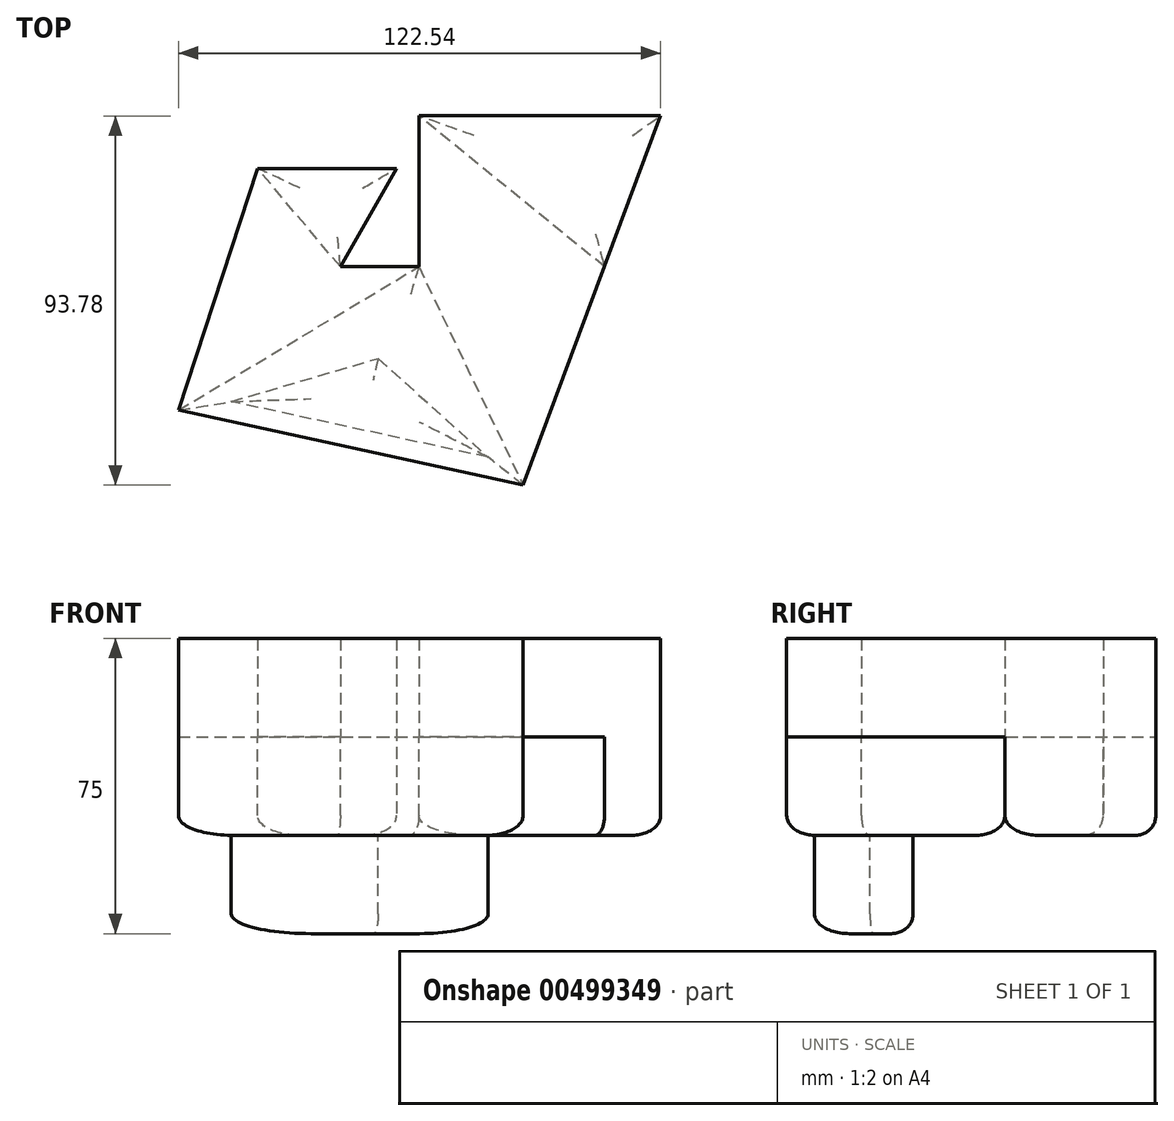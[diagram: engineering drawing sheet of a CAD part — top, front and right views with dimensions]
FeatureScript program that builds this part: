
annotation { "Feature Type Name" : "Feature", "Feature Type Description" : "" }
export const myFeature = defineFeature(function(context is Context, id is Id, definition is map)
    precondition{}
    {
        {
            var Q0;
            Q0=qCreatedBy(makeId("Top.planeOp"),FACE);
            var sketch = newSketch(context, id + "F0", { "sketchPlane" : qUnion([Q0])});
            skLineSegment(sketch, "E0", {"start": v(0, 0) * mm, "end": v(0, 38.34) * mm});
            skLineSegment(sketch, "E1", {"start": v(0, 38.34) * mm, "end": v(61.46, 38.34) * mm});
            skLineSegment(sketch, "E2", {"start": v(61.46, 38.34) * mm, "end": v(26.5, -55.44) * mm});
            skLineSegment(sketch, "E3", {"start": v(26.5, -55.44) * mm, "end": v(-61.08, -36.46) * mm});
            skLineSegment(sketch, "E4", {"start": v(-61.08, -36.46) * mm, "end": v(-40.97, 25) * mm});
            skLineSegment(sketch, "E5", {"start": v(-40.97, 25) * mm, "end": v(-5.64, 25) * mm});
            skLineSegment(sketch, "E6", {"start": v(-5.64, 25) * mm, "end": v(-19.92, 0) * mm});
            skLineSegment(sketch, "E7", {"start": v(-19.92, 0) * mm, "end": v(0, 0) * mm});
            skSolve(sketch);
        }
        {
            var Q0;
            Q0 = qSketchRegion(id + "F0", true);
            extrude(context, id + "F1", {"entities" : qUnion([Q0]), "depth" : 25 * mm});
        }
        {
            var Q0;
            Q0=makeQuery(id+"F1.opExtrude","CAP_FACE",FACE,{"disambiguationData":[OSD([sQuery(id+"F0.wireOp",EDGE,"E0"),sQuery(id+"F0.wireOp",EDGE,"E1"),sQuery(id+"F0.wireOp",EDGE,"E2"),sQuery(id+"F0.wireOp",EDGE,"E3"),sQuery(id+"F0.wireOp",EDGE,"E4"),sQuery(id+"F0.wireOp",EDGE,"E5"),sQuery(id+"F0.wireOp",EDGE,"E6"),sQuery(id+"F0.wireOp",EDGE,"E7")])],"isStart":true});
            var sketch = newSketch(context, id + "F2", { "sketchPlane" : qUnion([Q0])});
            skLineSegment(sketch, "E8", {"start": v(-61.08, 36.46) * mm, "end": v(0, 0) * mm});
            skLineSegment(sketch, "E9", {"start": v(0, 0) * mm, "end": v(26.5, 55.44) * mm});
            skLineSegment(sketch, "E10", {"start": v(-61.08, 36.46) * mm, "end": v(26.5, 55.44) * mm});
            skLineSegment(sketch, "E11", {"start": v(-19.92, 0) * mm, "end": v(-40.97, -25) * mm});
            skLineSegment(sketch, "E12", {"start": v(-40.97, -25) * mm, "end": v(-5.64, -25) * mm});
            skLineSegment(sketch, "E13", {"start": v(-5.64, -25) * mm, "end": v(-19.92, 0) * mm});
            skLineSegment(sketch, "E14", {"start": v(47.17, 0) * mm, "end": v(0, -38.34) * mm});
            skLineSegment(sketch, "E15", {"start": v(0, -38.34) * mm, "end": v(61.46, -38.34) * mm});
            skLineSegment(sketch, "E16", {"start": v(61.46, -38.34) * mm, "end": v(47.17, 0) * mm});
            skSolve(sketch);
        }
        {
            var Q0;
            Q0 = qSketchRegion(id + "F2", true);
            extrude(context, id + "F3", {"entities" : qUnion([Q0]), "operationType" : NewBodyOperationType.ADD, "depth" : 25 * mm});
        }
        {
            var Q0;
            Q0=makeQuery(id+"F3.opExtrude","CAP_EDGE",EDGE,{"disambiguationData":[OSD([sQuery(id+"F2.wireOp",EDGE,"E8")])],"isStart":false});
            var Q1;
            Q1=makeQuery(id+"F3.opExtrude","CAP_EDGE",EDGE,{"disambiguationData":[OSD([sQuery(id+"F2.wireOp",EDGE,"E9")])],"isStart":false});
            var Q2;
            Q2=makeQuery(id+"F3.opExtrude","CAP_EDGE",EDGE,{"disambiguationData":[OSD([sQuery(id+"F2.wireOp",EDGE,"E10")])],"isStart":false});
            fillet(context, id + "F4", {"entities" : qUnion([Q0, Q1, Q2]), "radius" : 5 * mm, "tangentPropagation" : true, "allowEdgeOverflow" : false});
        }
        {
            var Q0;
            Q0=makeQuery(id+"F3.opExtrude","CAP_EDGE",EDGE,{"disambiguationData":[OSD([sQuery(id+"F2.wireOp",EDGE,"E12")])],"isStart":false});
            var Q1;
            Q1=makeQuery(id+"F3.opExtrude","CAP_EDGE",EDGE,{"disambiguationData":[OSD([sQuery(id+"F2.wireOp",EDGE,"E11")])],"isStart":false});
            var Q2;
            Q2=makeQuery(id+"F3.opExtrude","CAP_EDGE",EDGE,{"disambiguationData":[OSD([sQuery(id+"F2.wireOp",EDGE,"E13")])],"isStart":false});
            fillet(context, id + "F5", {"entities" : qUnion([Q0, Q1, Q2]), "radius" : 5 * mm, "tangentPropagation" : true, "allowEdgeOverflow" : false});
        }
        {
            var Q0;
            Q0=makeQuery(id+"F3.opExtrude","CAP_EDGE",EDGE,{"disambiguationData":[OSD([sQuery(id+"F2.wireOp",EDGE,"E15")])],"isStart":false});
            var Q1;
            Q1=makeQuery(id+"F3.opExtrude","CAP_EDGE",EDGE,{"disambiguationData":[OSD([sQuery(id+"F2.wireOp",EDGE,"E16")])],"isStart":false});
            var Q2;
            Q2=makeQuery(id+"F3.opExtrude","CAP_EDGE",EDGE,{"disambiguationData":[OSD([sQuery(id+"F2.wireOp",EDGE,"E14")])],"isStart":false});
            fillet(context, id + "F6", {"entities" : qUnion([Q0, Q1, Q2]), "radius" : 5 * mm, "tangentPropagation" : true, "allowEdgeOverflow" : false});
        }
        {
            var Q0;
            Q0=makeQuery(id+"F3.opExtrude","CAP_FACE",FACE,{"disambiguationData":[OSD([sQuery(id+"F2.wireOp",EDGE,"E8"),sQuery(id+"F2.wireOp",EDGE,"E9"),sQuery(id+"F2.wireOp",EDGE,"E10")])],"isStart":false});
            var sketch = newSketch(context, id + "F7", { "sketchPlane" : qUnion([Q0])});
            skLineSegment(sketch, "E17", {"start": v(-47.64, 34.26) * mm, "end": v(-10.34, 23.3) * mm});
            skLineSegment(sketch, "E18", {"start": v(-10.34, 23.3) * mm, "end": v(17.6, 48.4) * mm});
            skLineSegment(sketch, "E19", {"start": v(17.6, 48.4) * mm, "end": v(-47.64, 34.26) * mm});
            skLineSegment(sketch, "E20", {"start": v(0, 0) * mm, "end": v(-10.34, 23.3) * mm});
            skSolve(sketch);
        }
        {
            var Q0;
            Q0 = qSketchRegion(id + "F7", true);
            extrude(context, id + "F8", {"entities" : qUnion([Q0]), "operationType" : NewBodyOperationType.ADD, "depth" : 25 * mm});
        }
        {
            var Q0;
            Q0=makeQuery(id+"F8.opExtrude","CAP_EDGE",EDGE,{"disambiguationData":[OSD([sQuery(id+"F7.wireOp",EDGE,"E17")])],"isStart":false});
            var Q1;
            Q1=makeQuery(id+"F8.opExtrude","CAP_EDGE",EDGE,{"disambiguationData":[OSD([sQuery(id+"F7.wireOp",EDGE,"E19")])],"isStart":false});
            var Q2;
            Q2=makeQuery(id+"F8.opExtrude","CAP_FACE",FACE,{"disambiguationData":[OSD([sQuery(id+"F7.wireOp",EDGE,"E17"),sQuery(id+"F7.wireOp",EDGE,"E18"),sQuery(id+"F7.wireOp",EDGE,"E19")])],"isStart":false});
            fillet(context, id + "F9", {"entities" : qUnion([Q0, Q1, Q2]), "radius" : 5 * mm, "tangentPropagation" : true, "allowEdgeOverflow" : false});
        }
    });
